# Revit family: Thorn AREAFLOOD L
name_source: partatom
category: Lighting Fixtures
revit_build: Autodesk Revit 2016 (Build: 20150220_1215(x64)
units: mm (PartAtom-declared; Revit-internal decimal feet)

## family parameters
Cut with Voids When Loaded = No
Host = Face
Light Source = Yes
OmniClass Number = 23.80.70.11
OmniClass Title = Luminaries for Internal Lighting
Part Type = Normal
Room Calculation Point = No
Round Connector Dimension = Use Diameter
Shared = No

## types (2) — shared parameters
Assembly Code = D5020200
Color Filter = 16777215
Description = LED flootlight
Dimming Lamp Color Temperature Shift = <None>
Height = 139 mm  [stored 0.456037 ft]
Lamp = LED
Length = 658 mm  [stored 2.15879 ft]
Manufacturer = Thorn Lighting
Tilt Angle = 0.00°
URL = http://www.thornlighting.com
Voltage = 230 V
Width = 490 mm  [stored 1.60761 ft]
zero-valued in all types: Default Elevation

## per-type parameters (varying)
| type | Apparent Load | Model | Photometric Web File |
| AFP L 120L70-740 A6 HFX CL2 GY | 249 VA | 96644594 | 96644594_(STD).IES |
| AFP L 144L70-740 A6 HFX CL2 GY | 297 VA | 96644682 | 96644682_(STD).IES |

note: [stored X ft] marks values corroborated as IEEE doubles in the binary element streams (Revit-internal decimal feet)

## geometry (parser evidence)
native form markers: Sweep x4
no freeform markers — native parametric forms only
